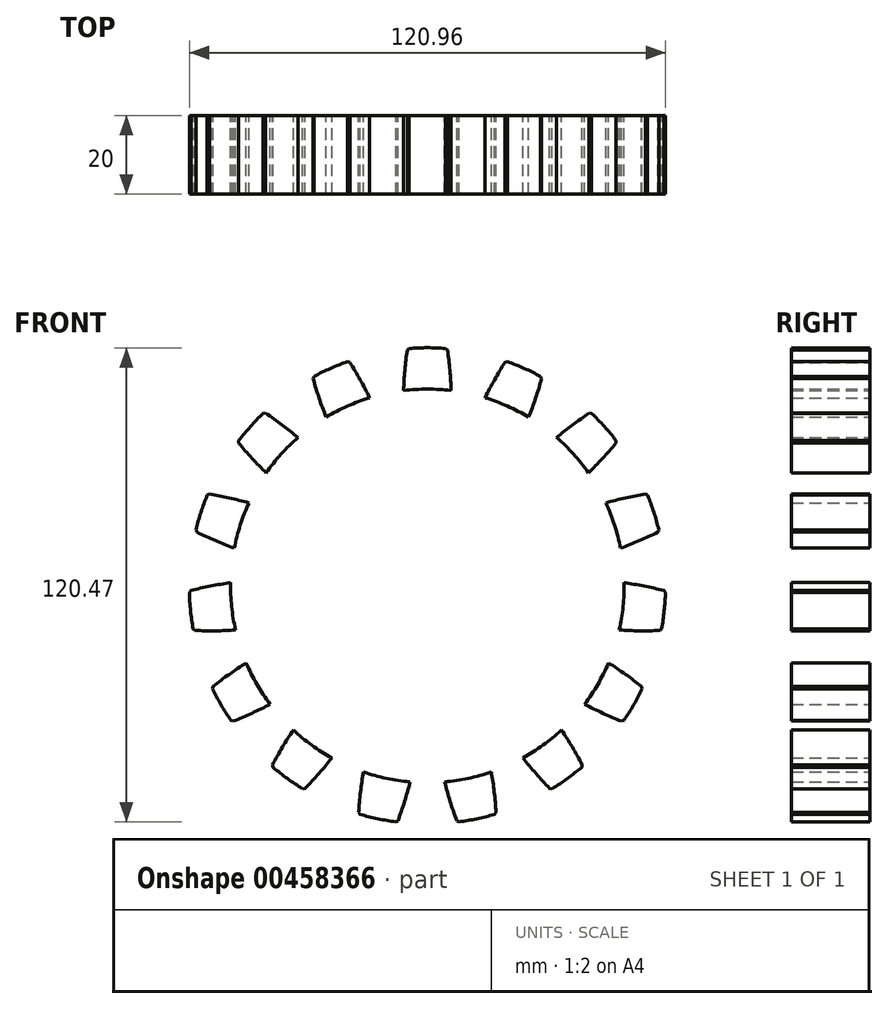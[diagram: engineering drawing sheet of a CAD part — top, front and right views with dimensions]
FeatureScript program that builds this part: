
annotation { "Feature Type Name" : "Feature", "Feature Type Description" : "" }
export const myFeature = defineFeature(function(context is Context, id is Id, definition is map)
    precondition{}
    {
        {
            var Q0;
            Q0=qCreatedBy(makeId("Front.planeOp"),FACE);
            var sketch = newSketch(context, id + "F0", { "sketchPlane" : qUnion([Q0])});
            skCircle(sketch, "E0", {"center": v(0, 0) * mm, "radius": 50 * mm});
            skLineSegment(sketch, "E1", {"start": v(0, 50) * mm, "end": v(0, 46.5) * mm, "construction": true});
            skLineSegment(sketch, "E2", {"start": v(0, 46.5) * mm, "end": v(83.9, 46.5) * mm, "construction": true});
            skArc(sketch, "E3", {"start": v(-5.04, 60.29) * mm, "mid": v(-5.7, 54.98) * mm, "end": v(-6.05, 49.63) * mm});
            skArc(sketch, "E4", {"start": v(5.04, 60.29) * mm, "mid": v(0, 60.5) * mm, "end": v(-5.04, 60.29) * mm});
            skArc(sketch, "E5.MirrorC", {"start": v(5.04, 60.29) * mm, "mid": v(5.83, 53.42) * mm, "end": v(6.1, 46.5) * mm});
            skArc(sketch, "E6.1.0", {"start": v(-29.12, 53.03) * mm, "mid": v(-27.57, 47.9) * mm, "end": v(-25.71, 42.88) * mm});
            skArc(sketch, "E6.1.1", {"start": v(-19.92, 57.13) * mm, "mid": v(-24.6, 55.27) * mm, "end": v(-29.12, 53.03) * mm});
            skArc(sketch, "E6.1.2", {"start": v(-19.92, 57.13) * mm, "mid": v(-16.4, 51.17) * mm, "end": v(-13.34, 44.96) * mm});
            skArc(sketch, "E6.2.0", {"start": v(-48.17, 36.6) * mm, "mid": v(-44.67, 32.55) * mm, "end": v(-40.93, 28.72) * mm});
            skArc(sketch, "E6.2.1", {"start": v(-41.43, 44.09) * mm, "mid": v(-44.96, 40.48) * mm, "end": v(-48.17, 36.6) * mm});
            skArc(sketch, "E6.2.2", {"start": v(-41.43, 44.09) * mm, "mid": v(-35.8, 40.08) * mm, "end": v(-30.47, 35.65) * mm});
            skArc(sketch, "E6.3.0", {"start": v(-58.9, 13.84) * mm, "mid": v(-54.05, 11.57) * mm, "end": v(-49.07, 9.59) * mm});
            skArc(sketch, "E6.3.1", {"start": v(-55.78, 23.42) * mm, "mid": v(-57.54, 18.7) * mm, "end": v(-58.9, 13.84) * mm});
            skArc(sketch, "E6.3.2", {"start": v(-55.78, 23.42) * mm, "mid": v(-49, 22.05) * mm, "end": v(-42.34, 20.17) * mm});
            skArc(sketch, "E6.4.0", {"start": v(-59.43, -11.31) * mm, "mid": v(-54.08, -11.42) * mm, "end": v(-48.73, -11.2) * mm});
            skArc(sketch, "E6.4.1", {"start": v(-60.49, -1.3) * mm, "mid": v(-60.17, -6.32) * mm, "end": v(-59.43, -11.31) * mm});
            skArc(sketch, "E6.4.2", {"start": v(-60.49, -1.3) * mm, "mid": v(-53.73, 0.22) * mm, "end": v(-46.88, 1.2) * mm});
            skArc(sketch, "E6.5.0", {"start": v(-49.7, -34.5) * mm, "mid": v(-44.76, -32.42) * mm, "end": v(-39.96, -30.05) * mm});
            skArc(sketch, "E6.5.1", {"start": v(-54.73, -25.78) * mm, "mid": v(-52.4, -30.25) * mm, "end": v(-49.7, -34.5) * mm});
            skArc(sketch, "E6.5.2", {"start": v(-54.73, -25.78) * mm, "mid": v(-49.18, -21.66) * mm, "end": v(-43.32, -17.97) * mm});
            skArc(sketch, "E6.6.0", {"start": v(-31.36, -51.74) * mm, "mid": v(-27.7, -47.83) * mm, "end": v(-24.28, -43.7) * mm});
            skArc(sketch, "E6.6.1", {"start": v(-39.51, -45.81) * mm, "mid": v(-35.56, -48.95) * mm, "end": v(-31.36, -51.74) * mm});
            skArc(sketch, "E6.6.2", {"start": v(-39.51, -45.81) * mm, "mid": v(-36.12, -39.78) * mm, "end": v(-32.27, -34.03) * mm});
            skArc(sketch, "E6.7.0", {"start": v(-7.6, -60.02) * mm, "mid": v(-5.85, -54.96) * mm, "end": v(-4.4, -49.8) * mm});
            skArc(sketch, "E6.7.1", {"start": v(-17.46, -57.93) * mm, "mid": v(-12.58, -59.18) * mm, "end": v(-7.6, -60.02) * mm});
            skArc(sketch, "E6.7.2", {"start": v(-17.46, -57.93) * mm, "mid": v(-16.81, -51.04) * mm, "end": v(-15.63, -44.22) * mm});
            skArc(sketch, "E6.8.0", {"start": v(17.46, -57.93) * mm, "mid": v(17, -52.6) * mm, "end": v(16.23, -47.3) * mm});
            skArc(sketch, "E6.8.1", {"start": v(7.6, -60.02) * mm, "mid": v(12.58, -59.18) * mm, "end": v(17.46, -57.93) * mm});
            skArc(sketch, "E6.8.2", {"start": v(7.6, -60.02) * mm, "mid": v(5.4, -53.46) * mm, "end": v(3.7, -46.75) * mm});
            skArc(sketch, "E6.9.0", {"start": v(39.51, -45.81) * mm, "mid": v(36.93, -41.13) * mm, "end": v(34.06, -36.6) * mm});
            skArc(sketch, "E6.9.1", {"start": v(31.36, -51.74) * mm, "mid": v(35.56, -48.95) * mm, "end": v(39.51, -45.81) * mm});
            skArc(sketch, "E6.9.2", {"start": v(31.36, -51.74) * mm, "mid": v(26.68, -46.64) * mm, "end": v(22.4, -41.2) * mm});
            skArc(sketch, "E7", {"start": v(2.05, 12.38) * mm, "mid": v(0, 12.55) * mm, "end": v(-2.05, 12.38) * mm});
            skLineSegment(sketch, "E8.left", {"start": v(0, 0) * mm, "end": v(0, -12.5) * mm});
            skLineSegment(sketch, "E8.right", {"start": v(2.05, 10.5) * mm, "end": v(2.05, -12.5) * mm});
            skLineSegment(sketch, "E9.left", {"start": v(2.05, 10.5) * mm, "end": v(2.05, 12.38) * mm});
            skLineSegment(sketch, "E10.MirrorCS", {"start": v(-2.05, 10.5) * mm, "end": v(-2.05, 12.38) * mm});
            skLineSegment(sketch, "E11.MirrorCS", {"start": v(-2.05, 10.5) * mm, "end": v(-2.05, -12.5) * mm});
            skPoint(sketch, "E12.MirrorCS.start.orphan", {"position": v(-2.05, 12.55) * mm});
            skPoint(sketch, "E13.orphan", {"position": v(0, 10.5) * mm});
            skPoint(sketch, "E14.orphan", {"position": v(-2.05, -12.5) * mm});
            skPoint(sketch, "E15.MirrorCS.start.orphan", {"position": v(0, -12.5) * mm});
            skArc(sketch, "E16.trimOffspring", {"start": v(-2.05, -12.38) * mm, "mid": v(0, -12.55) * mm, "end": v(2.05, -12.38) * mm});
            skArc(sketch, "E17.1.0", {"start": v(-5.62, 11.22) * mm, "mid": v(-7.38, 10.15) * mm, "end": v(-8.94, 8.81) * mm});
            skLineSegment(sketch, "E17.1.1", {"start": v(-4.51, 9.7) * mm, "end": v(-5.62, 11.22) * mm});
            skLineSegment(sketch, "E17.1.2", {"start": v(-7.83, 7.29) * mm, "end": v(-8.94, 8.81) * mm});
            skLineSegment(sketch, "E17.1.3", {"start": v(-7.83, 7.29) * mm, "end": v(5.69, -11.32) * mm});
            skLineSegment(sketch, "E17.1.4", {"start": v(-4.51, 9.7) * mm, "end": v(9, -8.9) * mm});
            skArc(sketch, "E17.1.5", {"start": v(5.62, -11.22) * mm, "mid": v(7.38, -10.15) * mm, "end": v(8.94, -8.81) * mm});
            skArc(sketch, "E17.2.0", {"start": v(-11.14, 5.78) * mm, "mid": v(-11.94, 3.88) * mm, "end": v(-12.4, 1.88) * mm});
            skLineSegment(sketch, "E17.2.1", {"start": v(-9.35, 5.2) * mm, "end": v(-11.14, 5.78) * mm});
            skLineSegment(sketch, "E17.2.2", {"start": v(-10.62, 1.3) * mm, "end": v(-12.4, 1.88) * mm});
            skLineSegment(sketch, "E17.2.3", {"start": v(-10.62, 1.3) * mm, "end": v(11.25, -5.81) * mm});
            skLineSegment(sketch, "E17.2.4", {"start": v(-9.35, 5.2) * mm, "end": v(12.52, -1.91) * mm});
            skArc(sketch, "E17.2.5", {"start": v(11.14, -5.78) * mm, "mid": v(11.94, -3.88) * mm, "end": v(12.4, -1.88) * mm});
            skArc(sketch, "E17.3.0", {"start": v(-12.4, -1.88) * mm, "mid": v(-11.94, -3.88) * mm, "end": v(-11.14, -5.78) * mm});
            skLineSegment(sketch, "E17.3.1", {"start": v(-10.62, -1.3) * mm, "end": v(-12.4, -1.88) * mm});
            skLineSegment(sketch, "E17.3.2", {"start": v(-9.35, -5.2) * mm, "end": v(-11.14, -5.78) * mm});
            skLineSegment(sketch, "E17.3.3", {"start": v(-9.35, -5.2) * mm, "end": v(12.52, 1.91) * mm});
            skLineSegment(sketch, "E17.3.4", {"start": v(-10.62, -1.3) * mm, "end": v(11.25, 5.81) * mm});
            skArc(sketch, "E17.3.5", {"start": v(12.4, 1.88) * mm, "mid": v(11.94, 3.88) * mm, "end": v(11.14, 5.78) * mm});
            skArc(sketch, "E17.4.0", {"start": v(-8.94, -8.81) * mm, "mid": v(-7.38, -10.15) * mm, "end": v(-5.62, -11.22) * mm});
            skLineSegment(sketch, "E17.4.1", {"start": v(-7.83, -7.29) * mm, "end": v(-8.94, -8.81) * mm});
            skLineSegment(sketch, "E17.4.2", {"start": v(-4.51, -9.7) * mm, "end": v(-5.62, -11.22) * mm});
            skLineSegment(sketch, "E17.4.3", {"start": v(-4.51, -9.7) * mm, "end": v(9, 8.9) * mm});
            skLineSegment(sketch, "E17.4.4", {"start": v(-7.83, -7.29) * mm, "end": v(5.69, 11.32) * mm});
            skArc(sketch, "E17.4.5", {"start": v(8.94, 8.81) * mm, "mid": v(7.38, 10.15) * mm, "end": v(5.62, 11.22) * mm});
            skLineSegment(sketch, "E17.5.1", {"start": v(-2.05, -10.5) * mm, "end": v(-2.05, -12.38) * mm});
            skLineSegment(sketch, "E17.5.2", {"start": v(2.05, -10.5) * mm, "end": v(2.05, -12.38) * mm});
            skLineSegment(sketch, "E17.5.3", {"start": v(2.05, -10.5) * mm, "end": v(2.05, 12.5) * mm});
            skLineSegment(sketch, "E17.5.4", {"start": v(-2.05, -10.5) * mm, "end": v(-2.05, 12.5) * mm});
            skArc(sketch, "E17.6.0", {"start": v(5.62, -11.22) * mm, "mid": v(7.38, -10.15) * mm, "end": v(8.94, -8.81) * mm});
            skLineSegment(sketch, "E17.6.1", {"start": v(4.51, -9.7) * mm, "end": v(5.62, -11.22) * mm});
            skLineSegment(sketch, "E17.6.2", {"start": v(7.83, -7.29) * mm, "end": v(8.94, -8.81) * mm});
            skLineSegment(sketch, "E17.6.3", {"start": v(7.83, -7.29) * mm, "end": v(-5.69, 11.32) * mm});
            skLineSegment(sketch, "E17.6.4", {"start": v(4.51, -9.7) * mm, "end": v(-9, 8.9) * mm});
            skArc(sketch, "E17.6.5", {"start": v(-5.62, 11.22) * mm, "mid": v(-7.38, 10.15) * mm, "end": v(-8.94, 8.81) * mm});
            skArc(sketch, "E17.7.0", {"start": v(11.14, -5.78) * mm, "mid": v(11.94, -3.88) * mm, "end": v(12.4, -1.88) * mm});
            skLineSegment(sketch, "E17.7.1", {"start": v(9.35, -5.2) * mm, "end": v(11.14, -5.78) * mm});
            skLineSegment(sketch, "E17.7.2", {"start": v(10.62, -1.3) * mm, "end": v(12.4, -1.88) * mm});
            skLineSegment(sketch, "E17.7.3", {"start": v(10.62, -1.3) * mm, "end": v(-11.25, 5.81) * mm});
            skLineSegment(sketch, "E17.7.4", {"start": v(9.35, -5.2) * mm, "end": v(-12.52, 1.91) * mm});
            skArc(sketch, "E17.7.5", {"start": v(-11.14, 5.78) * mm, "mid": v(-11.94, 3.88) * mm, "end": v(-12.4, 1.88) * mm});
            skArc(sketch, "E17.8.0", {"start": v(12.4, 1.88) * mm, "mid": v(11.94, 3.88) * mm, "end": v(11.14, 5.78) * mm});
            skLineSegment(sketch, "E17.8.1", {"start": v(10.62, 1.3) * mm, "end": v(12.4, 1.88) * mm});
            skLineSegment(sketch, "E17.8.2", {"start": v(9.35, 5.2) * mm, "end": v(11.14, 5.78) * mm});
            skLineSegment(sketch, "E17.8.3", {"start": v(9.35, 5.2) * mm, "end": v(-12.52, -1.91) * mm});
            skLineSegment(sketch, "E17.8.4", {"start": v(10.62, 1.3) * mm, "end": v(-11.25, -5.81) * mm});
            skArc(sketch, "E17.8.5", {"start": v(-12.4, -1.88) * mm, "mid": v(-11.94, -3.88) * mm, "end": v(-11.14, -5.78) * mm});
            skArc(sketch, "E17.9.0", {"start": v(8.94, 8.81) * mm, "mid": v(7.38, 10.15) * mm, "end": v(5.62, 11.22) * mm});
            skLineSegment(sketch, "E17.9.1", {"start": v(7.83, 7.29) * mm, "end": v(8.94, 8.81) * mm});
            skLineSegment(sketch, "E17.9.2", {"start": v(4.51, 9.7) * mm, "end": v(5.62, 11.22) * mm});
            skLineSegment(sketch, "E17.9.3", {"start": v(4.51, 9.7) * mm, "end": v(-9, -8.9) * mm});
            skLineSegment(sketch, "E17.9.4", {"start": v(7.83, 7.29) * mm, "end": v(-5.69, -11.32) * mm});
            skArc(sketch, "E17.9.5", {"start": v(-8.94, -8.81) * mm, "mid": v(-7.38, -10.15) * mm, "end": v(-5.62, -11.22) * mm});
            skCircle(sketch, "E18", {"center": v(0, 0) * mm, "radius": 10.5 * mm});
            skArc(sketch, "E19.3.10.0", {"start": v(54.73, -25.78) * mm, "mid": v(50.46, -22.55) * mm, "end": v(46, -19.58) * mm});
            skArc(sketch, "E19.4.10.0", {"start": v(49.7, -34.5) * mm, "mid": v(52.4, -30.25) * mm, "end": v(54.73, -25.78) * mm});
            skArc(sketch, "E19.8.10.0", {"start": v(49.7, -34.5) * mm, "mid": v(43.34, -31.76) * mm, "end": v(37.22, -28.53) * mm});
            skArc(sketch, "E19.3.11.0", {"start": v(60.49, -1.3) * mm, "mid": v(55.27, -0.08) * mm, "end": v(50, 0.82) * mm});
            skArc(sketch, "E19.4.11.0", {"start": v(59.43, -11.31) * mm, "mid": v(60.17, -6.32) * mm, "end": v(60.49, -1.3) * mm});
            skArc(sketch, "E19.8.11.0", {"start": v(59.43, -11.31) * mm, "mid": v(52.51, -11.39) * mm, "end": v(45.6, -10.93) * mm});
            skArc(sketch, "E19.3.12.0", {"start": v(55.78, 23.42) * mm, "mid": v(50.52, 22.4) * mm, "end": v(45.34, 21.09) * mm});
            skArc(sketch, "E19.4.12.0", {"start": v(58.9, 13.84) * mm, "mid": v(57.54, 18.7) * mm, "end": v(55.78, 23.42) * mm});
            skArc(sketch, "E19.8.12.0", {"start": v(58.9, 13.84) * mm, "mid": v(52.6, 10.96) * mm, "end": v(46.1, 8.57) * mm});
            skArc(sketch, "E19.3.13.0", {"start": v(41.43, 44.09) * mm, "mid": v(37.04, 41.02) * mm, "end": v(32.84, 37.7) * mm});
            skArc(sketch, "E19.4.13.0", {"start": v(48.17, 36.6) * mm, "mid": v(44.96, 40.48) * mm, "end": v(41.43, 44.09) * mm});
            skArc(sketch, "E19.8.13.0", {"start": v(48.17, 36.6) * mm, "mid": v(43.6, 31.4) * mm, "end": v(38.64, 26.58) * mm});
            skArc(sketch, "E19.3.14.0", {"start": v(19.92, 57.13) * mm, "mid": v(17.15, 52.54) * mm, "end": v(14.66, 47.8) * mm});
            skArc(sketch, "E19.4.14.0", {"start": v(29.12, 53.03) * mm, "mid": v(24.6, 55.27) * mm, "end": v(19.92, 57.13) * mm});
            skArc(sketch, "E19.8.14.0", {"start": v(29.12, 53.03) * mm, "mid": v(27.06, 46.42) * mm, "end": v(24.49, 40) * mm});
            skSolve(sketch);
        }
        {
            var Q0;
            Q0=makeQuery(id+"F0.imprint","IMPRINT",FACE,{"disambiguationData":[TD([[makeQuery(id+"F0.imprint","IMPRINT",EDGE,{"derivedFrom":sQuery(id+"F0.wireOp",EDGE,"E16.trimOffspring")}),-1.0]])]});
            var Q1;
            {var subQ0=sQuery(id+"F0.wireOp",EDGE,"E6.2.0");Q1=makeQuery(id+"F0.imprint","IMPRINT",FACE,{"disambiguationData":[TD([[makeQuery(id+"F0.imprint","IMPRINT",EDGE,{"derivedFrom":subQ0}),1.0]])]});}
            var Q2;
            {var subQ0=sQuery(id+"F0.wireOp",EDGE,"E6.1.0");Q2=makeQuery(id+"F0.imprint","IMPRINT",FACE,{"disambiguationData":[TD([[makeQuery(id+"F0.imprint","IMPRINT",EDGE,{"derivedFrom":subQ0}),1.0]])]});}
            var Q3;
            {var subQ0=sQuery(id+"F0.wireOp",EDGE,"E3");Q3=makeQuery(id+"F0.imprint","IMPRINT",FACE,{"disambiguationData":[TD([[makeQuery(id+"F0.imprint","IMPRINT",EDGE,{"derivedFrom":subQ0}),1.0]])]});}
            var Q4;
            {var subQ0=sQuery(id+"F0.wireOp",EDGE,"E6.9.0");Q4=makeQuery(id+"F0.imprint","IMPRINT",FACE,{"disambiguationData":[TD([[makeQuery(id+"F0.imprint","IMPRINT",EDGE,{"derivedFrom":subQ0}),1.0]])]});}
            var Q5;
            {var subQ0=sQuery(id+"F0.wireOp",EDGE,"E6.8.0");Q5=makeQuery(id+"F0.imprint","IMPRINT",FACE,{"disambiguationData":[TD([[makeQuery(id+"F0.imprint","IMPRINT",EDGE,{"derivedFrom":subQ0}),1.0]])]});}
            var Q6;
            {var subQ0=sQuery(id+"F0.wireOp",EDGE,"E6.7.0");Q6=makeQuery(id+"F0.imprint","IMPRINT",FACE,{"disambiguationData":[TD([[makeQuery(id+"F0.imprint","IMPRINT",EDGE,{"derivedFrom":subQ0}),1.0]])]});}
            var Q7;
            {var subQ0=sQuery(id+"F0.wireOp",EDGE,"E6.6.0");Q7=makeQuery(id+"F0.imprint","IMPRINT",FACE,{"disambiguationData":[TD([[makeQuery(id+"F0.imprint","IMPRINT",EDGE,{"derivedFrom":subQ0}),1.0]])]});}
            var Q8;
            {var subQ0=sQuery(id+"F0.wireOp",EDGE,"E6.5.0");Q8=makeQuery(id+"F0.imprint","IMPRINT",FACE,{"disambiguationData":[TD([[makeQuery(id+"F0.imprint","IMPRINT",EDGE,{"derivedFrom":subQ0}),1.0]])]});}
            var Q9;
            {var subQ0=sQuery(id+"F0.wireOp",EDGE,"E6.4.0");Q9=makeQuery(id+"F0.imprint","IMPRINT",FACE,{"disambiguationData":[TD([[makeQuery(id+"F0.imprint","IMPRINT",EDGE,{"derivedFrom":subQ0}),1.0]])]});}
            var Q10;
            {var subQ0=sQuery(id+"F0.wireOp",EDGE,"E6.3.0");Q10=makeQuery(id+"F0.imprint","IMPRINT",FACE,{"disambiguationData":[TD([[makeQuery(id+"F0.imprint","IMPRINT",EDGE,{"derivedFrom":subQ0}),1.0]])]});}
            var Q11;
            {var subQ0=sQuery(id+"F0.wireOp",EDGE,"E19.3.14.0");Q11=makeQuery(id+"F0.imprint","IMPRINT",FACE,{"disambiguationData":[TD([[makeQuery(id+"F0.imprint","IMPRINT",EDGE,{"derivedFrom":subQ0}),1.0]])]});}
            var Q12;
            {var subQ0=sQuery(id+"F0.wireOp",EDGE,"E19.3.13.0");Q12=makeQuery(id+"F0.imprint","IMPRINT",FACE,{"disambiguationData":[TD([[makeQuery(id+"F0.imprint","IMPRINT",EDGE,{"derivedFrom":subQ0}),1.0]])]});}
            var Q13;
            {var subQ0=sQuery(id+"F0.wireOp",EDGE,"E19.3.12.0");Q13=makeQuery(id+"F0.imprint","IMPRINT",FACE,{"disambiguationData":[TD([[makeQuery(id+"F0.imprint","IMPRINT",EDGE,{"derivedFrom":subQ0}),1.0]])]});}
            var Q14;
            {var subQ0=sQuery(id+"F0.wireOp",EDGE,"E19.3.11.0");Q14=makeQuery(id+"F0.imprint","IMPRINT",FACE,{"disambiguationData":[TD([[makeQuery(id+"F0.imprint","IMPRINT",EDGE,{"derivedFrom":subQ0}),1.0]])]});}
            var Q15;
            {var subQ0=sQuery(id+"F0.wireOp",EDGE,"E19.3.10.0");Q15=makeQuery(id+"F0.imprint","IMPRINT",FACE,{"disambiguationData":[TD([[makeQuery(id+"F0.imprint","IMPRINT",EDGE,{"derivedFrom":subQ0}),1.0]])]});}
            extrude(context, id + "F1", {"entities" : qUnion([Q0, Q1, Q2, Q3, Q4, Q5, Q6, Q7, Q8, Q9, Q10, Q11, Q12, Q13, Q14, Q15]), "depth" : 20 * mm});
        }
        {
            var Q0;
            Q0=makeQuery(id+"F1.opExtrude","SWEPT_EDGE",EDGE,{"disambiguationData":[OSD([sQuery(id+"F0.wireOp",EDGE,"E4"),sQuery(id+"F0.wireOp",EDGE,"E5.MirrorC")])]});
            var Q1;
            Q1=makeQuery(id+"F1.opExtrude","SWEPT_EDGE",EDGE,{"disambiguationData":[OSD([sQuery(id+"F0.wireOp",EDGE,"E19.3.14.0"),sQuery(id+"F0.wireOp",EDGE,"E19.4.14.0")])]});
            var Q2;
            Q2=makeQuery(id+"F1.opExtrude","SWEPT_EDGE",EDGE,{"disambiguationData":[OSD([sQuery(id+"F0.wireOp",EDGE,"E19.4.14.0"),sQuery(id+"F0.wireOp",EDGE,"E19.8.14.0")])]});
            var Q3;
            Q3=makeQuery(id+"F1.opExtrude","SWEPT_EDGE",EDGE,{"disambiguationData":[OSD([sQuery(id+"F0.wireOp",EDGE,"E19.3.13.0"),sQuery(id+"F0.wireOp",EDGE,"E19.4.13.0")])]});
            var Q4;
            Q4=makeQuery(id+"F1.opExtrude","SWEPT_EDGE",EDGE,{"disambiguationData":[OSD([sQuery(id+"F0.wireOp",EDGE,"E19.4.13.0"),sQuery(id+"F0.wireOp",EDGE,"E19.8.13.0")])]});
            var Q5;
            Q5=makeQuery(id+"F1.opExtrude","SWEPT_EDGE",EDGE,{"disambiguationData":[OSD([sQuery(id+"F0.wireOp",EDGE,"E19.3.12.0"),sQuery(id+"F0.wireOp",EDGE,"E19.4.12.0")])]});
            var Q6;
            Q6=makeQuery(id+"F1.opExtrude","SWEPT_EDGE",EDGE,{"disambiguationData":[OSD([sQuery(id+"F0.wireOp",EDGE,"E19.4.12.0"),sQuery(id+"F0.wireOp",EDGE,"E19.8.12.0")])]});
            var Q7;
            Q7=makeQuery(id+"F1.opExtrude","SWEPT_EDGE",EDGE,{"disambiguationData":[OSD([sQuery(id+"F0.wireOp",EDGE,"E19.3.11.0"),sQuery(id+"F0.wireOp",EDGE,"E19.4.11.0")])]});
            var Q8;
            Q8=makeQuery(id+"F1.opExtrude","SWEPT_EDGE",EDGE,{"disambiguationData":[OSD([sQuery(id+"F0.wireOp",EDGE,"E19.4.11.0"),sQuery(id+"F0.wireOp",EDGE,"E19.8.11.0")])]});
            var Q9;
            Q9=makeQuery(id+"F1.opExtrude","SWEPT_EDGE",EDGE,{"disambiguationData":[OSD([sQuery(id+"F0.wireOp",EDGE,"E19.3.10.0"),sQuery(id+"F0.wireOp",EDGE,"E19.4.10.0")])]});
            var Q10;
            Q10=makeQuery(id+"F1.opExtrude","SWEPT_EDGE",EDGE,{"disambiguationData":[OSD([sQuery(id+"F0.wireOp",EDGE,"E19.4.10.0"),sQuery(id+"F0.wireOp",EDGE,"E19.8.10.0")])]});
            var Q11;
            Q11=makeQuery(id+"F1.opExtrude","SWEPT_EDGE",EDGE,{"disambiguationData":[OSD([sQuery(id+"F0.wireOp",EDGE,"E6.9.0"),sQuery(id+"F0.wireOp",EDGE,"E6.9.1")])]});
            var Q12;
            Q12=makeQuery(id+"F1.opExtrude","SWEPT_EDGE",EDGE,{"disambiguationData":[OSD([sQuery(id+"F0.wireOp",EDGE,"E6.9.1"),sQuery(id+"F0.wireOp",EDGE,"E6.9.2")])]});
            var Q13;
            Q13=makeQuery(id+"F1.opExtrude","SWEPT_EDGE",EDGE,{"disambiguationData":[OSD([sQuery(id+"F0.wireOp",EDGE,"E6.8.0"),sQuery(id+"F0.wireOp",EDGE,"E6.8.1")])]});
            var Q14;
            Q14=makeQuery(id+"F1.opExtrude","SWEPT_EDGE",EDGE,{"disambiguationData":[OSD([sQuery(id+"F0.wireOp",EDGE,"E6.8.1"),sQuery(id+"F0.wireOp",EDGE,"E6.8.2")])]});
            var Q15;
            Q15=makeQuery(id+"F1.opExtrude","SWEPT_EDGE",EDGE,{"disambiguationData":[OSD([sQuery(id+"F0.wireOp",EDGE,"E6.7.0"),sQuery(id+"F0.wireOp",EDGE,"E6.7.1")])]});
            var Q16;
            Q16=makeQuery(id+"F1.opExtrude","SWEPT_EDGE",EDGE,{"disambiguationData":[OSD([sQuery(id+"F0.wireOp",EDGE,"E6.7.1"),sQuery(id+"F0.wireOp",EDGE,"E6.7.2")])]});
            var Q17;
            Q17=makeQuery(id+"F1.opExtrude","SWEPT_EDGE",EDGE,{"disambiguationData":[OSD([sQuery(id+"F0.wireOp",EDGE,"E6.6.0"),sQuery(id+"F0.wireOp",EDGE,"E6.6.1")])]});
            var Q18;
            Q18=makeQuery(id+"F1.opExtrude","SWEPT_EDGE",EDGE,{"disambiguationData":[OSD([sQuery(id+"F0.wireOp",EDGE,"E6.6.1"),sQuery(id+"F0.wireOp",EDGE,"E6.6.2")])]});
            var Q19;
            Q19=makeQuery(id+"F1.opExtrude","SWEPT_EDGE",EDGE,{"disambiguationData":[OSD([sQuery(id+"F0.wireOp",EDGE,"E6.5.0"),sQuery(id+"F0.wireOp",EDGE,"E6.5.1")])]});
            var Q20;
            Q20=makeQuery(id+"F1.opExtrude","SWEPT_EDGE",EDGE,{"disambiguationData":[OSD([sQuery(id+"F0.wireOp",EDGE,"E6.5.1"),sQuery(id+"F0.wireOp",EDGE,"E6.5.2")])]});
            var Q21;
            Q21=makeQuery(id+"F1.opExtrude","SWEPT_EDGE",EDGE,{"disambiguationData":[OSD([sQuery(id+"F0.wireOp",EDGE,"E6.4.0"),sQuery(id+"F0.wireOp",EDGE,"E6.4.1")])]});
            var Q22;
            Q22=makeQuery(id+"F1.opExtrude","SWEPT_EDGE",EDGE,{"disambiguationData":[OSD([sQuery(id+"F0.wireOp",EDGE,"E3"),sQuery(id+"F0.wireOp",EDGE,"E4")])]});
            var Q23;
            Q23=makeQuery(id+"F1.opExtrude","SWEPT_EDGE",EDGE,{"disambiguationData":[OSD([sQuery(id+"F0.wireOp",EDGE,"E6.1.1"),sQuery(id+"F0.wireOp",EDGE,"E6.1.2")])]});
            var Q24;
            Q24=makeQuery(id+"F1.opExtrude","SWEPT_EDGE",EDGE,{"disambiguationData":[OSD([sQuery(id+"F0.wireOp",EDGE,"E6.1.0"),sQuery(id+"F0.wireOp",EDGE,"E6.1.1")])]});
            var Q25;
            Q25=makeQuery(id+"F1.opExtrude","SWEPT_EDGE",EDGE,{"disambiguationData":[OSD([sQuery(id+"F0.wireOp",EDGE,"E6.2.1"),sQuery(id+"F0.wireOp",EDGE,"E6.2.2")])]});
            var Q26;
            Q26=makeQuery(id+"F1.opExtrude","SWEPT_EDGE",EDGE,{"disambiguationData":[OSD([sQuery(id+"F0.wireOp",EDGE,"E6.2.0"),sQuery(id+"F0.wireOp",EDGE,"E6.2.1")])]});
            var Q27;
            Q27=makeQuery(id+"F1.opExtrude","SWEPT_EDGE",EDGE,{"disambiguationData":[OSD([sQuery(id+"F0.wireOp",EDGE,"E6.3.1"),sQuery(id+"F0.wireOp",EDGE,"E6.3.2")])]});
            var Q28;
            Q28=makeQuery(id+"F1.opExtrude","SWEPT_EDGE",EDGE,{"disambiguationData":[OSD([sQuery(id+"F0.wireOp",EDGE,"E6.3.0"),sQuery(id+"F0.wireOp",EDGE,"E6.3.1")])]});
            var Q29;
            Q29=makeQuery(id+"F1.opExtrude","SWEPT_EDGE",EDGE,{"disambiguationData":[OSD([sQuery(id+"F0.wireOp",EDGE,"E6.4.1"),sQuery(id+"F0.wireOp",EDGE,"E6.4.2")])]});
            chamfer(context, id + "F2", {"entities" : qUnion([Q0, Q1, Q2, Q3, Q4, Q5, Q6, Q7, Q8, Q9, Q10, Q11, Q12, Q13, Q14, Q15, Q16, Q17, Q18, Q19, Q20, Q21, Q22, Q23, Q24, Q25, Q26, Q27, Q28, Q29]), "width" : 0.5 * mm, "tangentPropagation" : true});
        }
        {
            var Q0;
            Q0=makeQuery(id+"F1.opExtrude","SWEPT_BODY",BODY,{"disambiguationData":[OSD([sQuery(id+"F0.wireOp",EDGE,"E0"),sQuery(id+"F0.wireOp",EDGE,"E3"),sQuery(id+"F0.wireOp",EDGE,"E4"),sQuery(id+"F0.wireOp",EDGE,"E5.MirrorC"),sQuery(id+"F0.wireOp",EDGE,"E6.1.0"),sQuery(id+"F0.wireOp",EDGE,"E6.1.1"),sQuery(id+"F0.wireOp",EDGE,"E6.1.2"),sQuery(id+"F0.wireOp",EDGE,"E6.2.0"),sQuery(id+"F0.wireOp",EDGE,"E6.2.1"),sQuery(id+"F0.wireOp",EDGE,"E6.2.2"),sQuery(id+"F0.wireOp",EDGE,"E6.3.0"),sQuery(id+"F0.wireOp",EDGE,"E6.3.1"),sQuery(id+"F0.wireOp",EDGE,"E6.3.2"),sQuery(id+"F0.wireOp",EDGE,"E6.4.0"),sQuery(id+"F0.wireOp",EDGE,"E6.4.1"),sQuery(id+"F0.wireOp",EDGE,"E6.4.2"),sQuery(id+"F0.wireOp",EDGE,"E6.5.0"),sQuery(id+"F0.wireOp",EDGE,"E6.5.1"),sQuery(id+"F0.wireOp",EDGE,"E6.5.2"),sQuery(id+"F0.wireOp",EDGE,"E6.6.0"),sQuery(id+"F0.wireOp",EDGE,"E6.6.1"),sQuery(id+"F0.wireOp",EDGE,"E6.6.2"),sQuery(id+"F0.wireOp",EDGE,"E6.7.0"),sQuery(id+"F0.wireOp",EDGE,"E6.7.1"),sQuery(id+"F0.wireOp",EDGE,"E6.7.2"),sQuery(id+"F0.wireOp",EDGE,"E6.8.0"),sQuery(id+"F0.wireOp",EDGE,"E6.8.1"),sQuery(id+"F0.wireOp",EDGE,"E6.8.2"),sQuery(id+"F0.wireOp",EDGE,"E6.9.0"),sQuery(id+"F0.wireOp",EDGE,"E6.9.1"),sQuery(id+"F0.wireOp",EDGE,"E6.9.2"),sQuery(id+"F0.wireOp",EDGE,"E16.trimOffspring"),sQuery(id+"F0.wireOp",EDGE,"E17.5.1"),sQuery(id+"F0.wireOp",EDGE,"E17.5.2"),sQuery(id+"F0.wireOp",EDGE,"E17.5.3"),sQuery(id+"F0.wireOp",EDGE,"E17.5.4"),sQuery(id+"F0.wireOp",EDGE,"E7"),sQuery(id+"F0.wireOp",EDGE,"E17.6.0"),sQuery(id+"F0.wireOp",EDGE,"E17.6.1"),sQuery(id+"F0.wireOp",EDGE,"E17.6.2"),sQuery(id+"F0.wireOp",EDGE,"E17.6.3"),sQuery(id+"F0.wireOp",EDGE,"E17.6.4"),sQuery(id+"F0.wireOp",EDGE,"E17.6.5"),sQuery(id+"F0.wireOp",EDGE,"E17.7.0"),sQuery(id+"F0.wireOp",EDGE,"E17.7.1"),sQuery(id+"F0.wireOp",EDGE,"E17.7.2"),sQuery(id+"F0.wireOp",EDGE,"E17.7.3"),sQuery(id+"F0.wireOp",EDGE,"E17.7.4"),sQuery(id+"F0.wireOp",EDGE,"E17.7.5"),sQuery(id+"F0.wireOp",EDGE,"E17.8.0"),sQuery(id+"F0.wireOp",EDGE,"E17.8.1"),sQuery(id+"F0.wireOp",EDGE,"E17.8.2"),sQuery(id+"F0.wireOp",EDGE,"E17.8.3"),sQuery(id+"F0.wireOp",EDGE,"E17.8.4"),sQuery(id+"F0.wireOp",EDGE,"E17.8.5"),sQuery(id+"F0.wireOp",EDGE,"E17.9.0"),sQuery(id+"F0.wireOp",EDGE,"E17.9.1"),sQuery(id+"F0.wireOp",EDGE,"E17.9.2"),sQuery(id+"F0.wireOp",EDGE,"E17.9.3"),sQuery(id+"F0.wireOp",EDGE,"E17.9.4"),sQuery(id+"F0.wireOp",EDGE,"E17.9.5"),sQuery(id+"F0.wireOp",EDGE,"E18"),sQuery(id+"F0.wireOp",EDGE,"E19.3.10.0"),sQuery(id+"F0.wireOp",EDGE,"E19.4.10.0"),sQuery(id+"F0.wireOp",EDGE,"E19.8.10.0"),sQuery(id+"F0.wireOp",EDGE,"E19.3.11.0"),sQuery(id+"F0.wireOp",EDGE,"E19.4.11.0"),sQuery(id+"F0.wireOp",EDGE,"E19.8.11.0"),sQuery(id+"F0.wireOp",EDGE,"E19.3.12.0"),sQuery(id+"F0.wireOp",EDGE,"E19.4.12.0"),sQuery(id+"F0.wireOp",EDGE,"E19.8.12.0"),sQuery(id+"F0.wireOp",EDGE,"E19.3.13.0"),sQuery(id+"F0.wireOp",EDGE,"E19.4.13.0"),sQuery(id+"F0.wireOp",EDGE,"E19.8.13.0"),sQuery(id+"F0.wireOp",EDGE,"E19.3.14.0"),sQuery(id+"F0.wireOp",EDGE,"E19.4.14.0"),sQuery(id+"F0.wireOp",EDGE,"E19.8.14.0")])]});
            transform(context, id + "F3", {"entities" : qUnion([Q0]), "transformType" : TransformType.TRANSLATION_3D, "dx" : 0 * mm, "dy" : 0 * mm, "dz" : 0 * mm, "makeCopy" : true});
        }
    });
